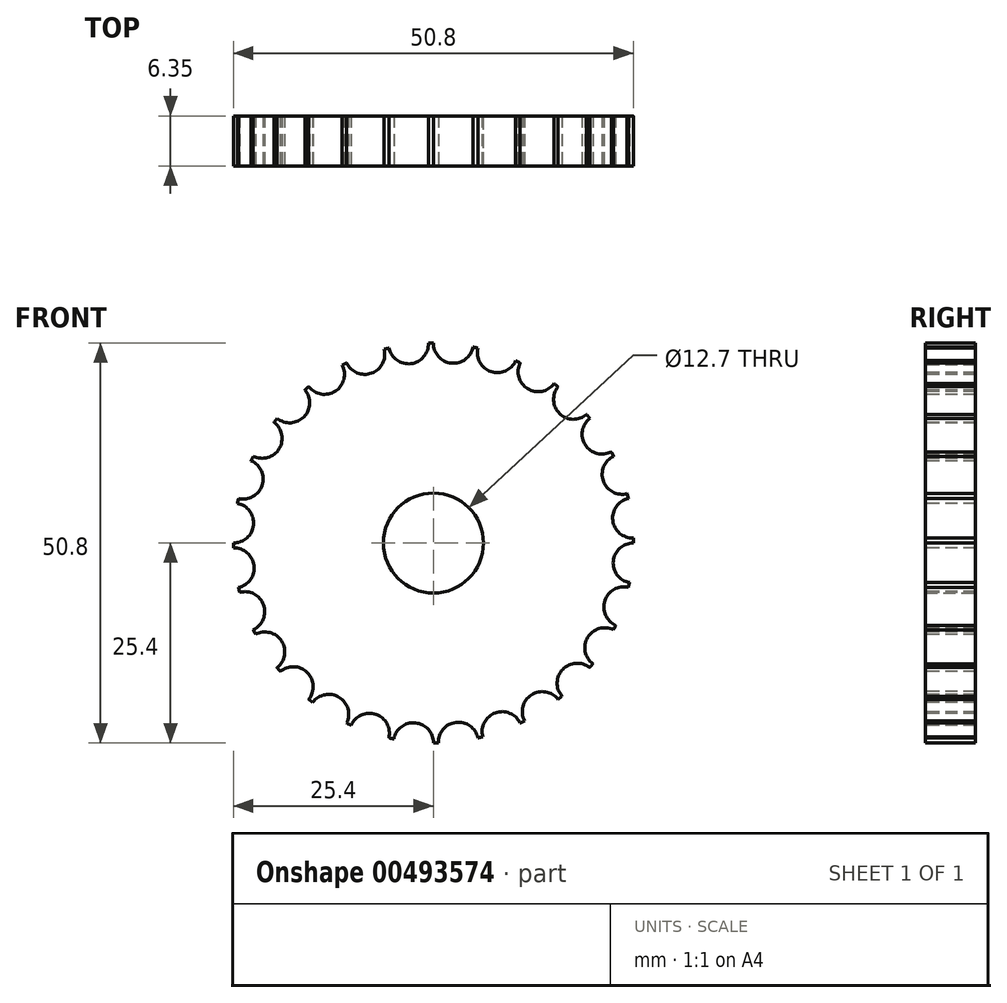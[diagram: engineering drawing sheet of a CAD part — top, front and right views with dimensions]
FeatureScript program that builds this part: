
annotation { "Feature Type Name" : "Feature", "Feature Type Description" : "" }
export const myFeature = defineFeature(function(context is Context, id is Id, definition is map)
    precondition{}
    {
        {
            var Q0;
            Q0=qCreatedBy(makeId("Front.planeOp"),FACE);
            var sketch = newSketch(context, id + "F0", { "sketchPlane" : qUnion([Q0])});
            skCircle(sketch, "E0", {"center": v(0, 0) * mm, "radius": 6.35 * mm});
            skCircle(sketch, "E1", {"center": v(0, 0) * mm, "radius": 25.4 * mm});
            skSolve(sketch);
        }
        {
            var Q0;
            Q0 = qSketchRegion(id + "F0", true);
            extrude(context, id + "F1", {"entities" : qUnion([Q0]), "depth" : 6.35 * mm, "offsetDistance" : 25.4 * mm});
        }
        {
            var Q0;
            Q0=makeQuery(id+"F1.opExtrude","CAP_FACE",FACE,{"disambiguationData":[OSD([sQuery(id+"F0.wireOp",EDGE,"E0"),sQuery(id+"F0.wireOp",EDGE,"E1")])],"isStart":false});
            var sketch = newSketch(context, id + "F2", { "sketchPlane" : qUnion([Q0])});
            skArc(sketch, "E2", {"start": v(0, 25.4) * mm, "mid": v(2.29, 22.85) * mm, "end": v(5.03, 24.9) * mm});
            skCircle(sketch, "E3", {"center": v(0, 0) * mm, "radius": 25.4 * mm});
            skArc(sketch, "E4.1.0", {"start": v(-5.65, 24.76) * mm, "mid": v(-2.86, 22.79) * mm, "end": v(-0.63, 25.4) * mm});
            skArc(sketch, "E4.2.0", {"start": v(-11.02, 22.88) * mm, "mid": v(-7.85, 21.58) * mm, "end": v(-6.27, 24.61) * mm});
            skArc(sketch, "E4.3.0", {"start": v(-15.84, 19.86) * mm, "mid": v(-12.46, 19.3) * mm, "end": v(-11.59, 22.6) * mm});
            skArc(sketch, "E4.4.0", {"start": v(-19.86, 15.84) * mm, "mid": v(-16.44, 16.04) * mm, "end": v(-16.33, 19.46) * mm});
            skArc(sketch, "E4.5.0", {"start": v(-22.88, 11.02) * mm, "mid": v(-19.6, 11.98) * mm, "end": v(-20.25, 15.34) * mm});
            skArc(sketch, "E4.6.0", {"start": v(-24.76, 5.65) * mm, "mid": v(-21.77, 7.31) * mm, "end": v(-23.15, 10.45) * mm});
            skArc(sketch, "E4.7.0", {"start": v(-25.4, 0) * mm, "mid": v(-22.85, 2.29) * mm, "end": v(-24.9, 5.03) * mm});
            skArc(sketch, "E4.8.0", {"start": v(-24.76, -5.65) * mm, "mid": v(-22.79, -2.86) * mm, "end": v(-25.4, -0.63) * mm});
            skArc(sketch, "E4.9.0", {"start": v(-22.88, -11.02) * mm, "mid": v(-21.58, -7.85) * mm, "end": v(-24.61, -6.27) * mm});
            skArc(sketch, "E4.10.0", {"start": v(-19.86, -15.84) * mm, "mid": v(-19.3, -12.46) * mm, "end": v(-22.6, -11.59) * mm});
            skArc(sketch, "E4.11.0", {"start": v(-15.84, -19.86) * mm, "mid": v(-16.04, -16.44) * mm, "end": v(-19.46, -16.33) * mm});
            skArc(sketch, "E4.12.0", {"start": v(-11.02, -22.88) * mm, "mid": v(-11.98, -19.6) * mm, "end": v(-15.34, -20.25) * mm});
            skArc(sketch, "E4.13.0", {"start": v(-5.65, -24.76) * mm, "mid": v(-7.31, -21.77) * mm, "end": v(-10.45, -23.15) * mm});
            skArc(sketch, "E4.14.0", {"start": v(0, -25.4) * mm, "mid": v(-2.29, -22.85) * mm, "end": v(-5.03, -24.9) * mm});
            skArc(sketch, "E4.15.0", {"start": v(5.65, -24.76) * mm, "mid": v(2.86, -22.79) * mm, "end": v(0.63, -25.4) * mm});
            skArc(sketch, "E4.16.0", {"start": v(11.02, -22.88) * mm, "mid": v(7.85, -21.58) * mm, "end": v(6.27, -24.61) * mm});
            skArc(sketch, "E4.17.0", {"start": v(15.84, -19.86) * mm, "mid": v(12.46, -19.3) * mm, "end": v(11.59, -22.6) * mm});
            skArc(sketch, "E4.18.0", {"start": v(19.86, -15.84) * mm, "mid": v(16.44, -16.04) * mm, "end": v(16.33, -19.46) * mm});
            skArc(sketch, "E4.19.0", {"start": v(22.88, -11.02) * mm, "mid": v(19.6, -11.98) * mm, "end": v(20.25, -15.34) * mm});
            skArc(sketch, "E4.20.0", {"start": v(24.76, -5.65) * mm, "mid": v(21.77, -7.31) * mm, "end": v(23.15, -10.45) * mm});
            skArc(sketch, "E4.21.0", {"start": v(25.4, 0) * mm, "mid": v(22.85, -2.29) * mm, "end": v(24.9, -5.03) * mm});
            skArc(sketch, "E5.2.22.0", {"start": v(24.76, 5.65) * mm, "mid": v(22.79, 2.86) * mm, "end": v(25.4, 0.63) * mm});
            skArc(sketch, "E6.2.23.0", {"start": v(22.88, 11.02) * mm, "mid": v(21.58, 7.85) * mm, "end": v(24.61, 6.27) * mm});
            skArc(sketch, "E7.2.24.0", {"start": v(19.86, 15.84) * mm, "mid": v(19.3, 12.46) * mm, "end": v(22.6, 11.59) * mm});
            skArc(sketch, "E8.2.25.0", {"start": v(15.84, 19.86) * mm, "mid": v(16.04, 16.44) * mm, "end": v(19.46, 16.33) * mm});
            skArc(sketch, "E9.2.26.0", {"start": v(11.02, 22.88) * mm, "mid": v(11.98, 19.6) * mm, "end": v(15.34, 20.25) * mm});
            skArc(sketch, "E9.2.27.0", {"start": v(5.65, 24.76) * mm, "mid": v(7.31, 21.77) * mm, "end": v(10.45, 23.15) * mm});
            skSolve(sketch);
        }
        {
            var Q0;
            {var subQ0=sQuery(id+"F2.wireOp",EDGE,"E4.1.0");Q0=makeQuery(id+"F2.imprint","IMPRINT",FACE,{"disambiguationData":[TD([[makeQuery(id+"F2.imprint","IMPRINT",EDGE,{"derivedFrom":subQ0}),1.0]])]});}
            var Q1;
            {var subQ0=sQuery(id+"F2.wireOp",EDGE,"E2");Q1=makeQuery(id+"F2.imprint","IMPRINT",FACE,{"disambiguationData":[TD([[makeQuery(id+"F2.imprint","IMPRINT",EDGE,{"derivedFrom":subQ0}),1.0]])]});}
            var Q2;
            {var subQ0=sQuery(id+"F2.wireOp",EDGE,"E4.21.0");Q2=makeQuery(id+"F2.imprint","IMPRINT",FACE,{"disambiguationData":[TD([[makeQuery(id+"F2.imprint","IMPRINT",EDGE,{"derivedFrom":subQ0}),1.0]])]});}
            var Q3;
            {var subQ0=sQuery(id+"F2.wireOp",EDGE,"E4.20.0");Q3=makeQuery(id+"F2.imprint","IMPRINT",FACE,{"disambiguationData":[TD([[makeQuery(id+"F2.imprint","IMPRINT",EDGE,{"derivedFrom":subQ0}),1.0]])]});}
            var Q4;
            {var subQ0=sQuery(id+"F2.wireOp",EDGE,"E4.19.0");Q4=makeQuery(id+"F2.imprint","IMPRINT",FACE,{"disambiguationData":[TD([[makeQuery(id+"F2.imprint","IMPRINT",EDGE,{"derivedFrom":subQ0}),1.0]])]});}
            var Q5;
            {var subQ0=sQuery(id+"F2.wireOp",EDGE,"E4.18.0");Q5=makeQuery(id+"F2.imprint","IMPRINT",FACE,{"disambiguationData":[TD([[makeQuery(id+"F2.imprint","IMPRINT",EDGE,{"derivedFrom":subQ0}),1.0]])]});}
            var Q6;
            {var subQ0=sQuery(id+"F2.wireOp",EDGE,"E4.17.0");Q6=makeQuery(id+"F2.imprint","IMPRINT",FACE,{"disambiguationData":[TD([[makeQuery(id+"F2.imprint","IMPRINT",EDGE,{"derivedFrom":subQ0}),1.0]])]});}
            var Q7;
            {var subQ0=sQuery(id+"F2.wireOp",EDGE,"E4.16.0");Q7=makeQuery(id+"F2.imprint","IMPRINT",FACE,{"disambiguationData":[TD([[makeQuery(id+"F2.imprint","IMPRINT",EDGE,{"derivedFrom":subQ0}),1.0]])]});}
            var Q8;
            {var subQ0=sQuery(id+"F2.wireOp",EDGE,"E4.15.0");Q8=makeQuery(id+"F2.imprint","IMPRINT",FACE,{"disambiguationData":[TD([[makeQuery(id+"F2.imprint","IMPRINT",EDGE,{"derivedFrom":subQ0}),1.0]])]});}
            var Q9;
            {var subQ0=sQuery(id+"F2.wireOp",EDGE,"E4.14.0");Q9=makeQuery(id+"F2.imprint","IMPRINT",FACE,{"disambiguationData":[TD([[makeQuery(id+"F2.imprint","IMPRINT",EDGE,{"derivedFrom":subQ0}),1.0]])]});}
            var Q10;
            {var subQ0=sQuery(id+"F2.wireOp",EDGE,"E4.13.0");Q10=makeQuery(id+"F2.imprint","IMPRINT",FACE,{"disambiguationData":[TD([[makeQuery(id+"F2.imprint","IMPRINT",EDGE,{"derivedFrom":subQ0}),1.0]])]});}
            var Q11;
            {var subQ0=sQuery(id+"F2.wireOp",EDGE,"E4.12.0");Q11=makeQuery(id+"F2.imprint","IMPRINT",FACE,{"disambiguationData":[TD([[makeQuery(id+"F2.imprint","IMPRINT",EDGE,{"derivedFrom":subQ0}),1.0]])]});}
            var Q12;
            {var subQ0=sQuery(id+"F2.wireOp",EDGE,"E4.11.0");Q12=makeQuery(id+"F2.imprint","IMPRINT",FACE,{"disambiguationData":[TD([[makeQuery(id+"F2.imprint","IMPRINT",EDGE,{"derivedFrom":subQ0}),1.0]])]});}
            var Q13;
            {var subQ0=sQuery(id+"F2.wireOp",EDGE,"E4.10.0");Q13=makeQuery(id+"F2.imprint","IMPRINT",FACE,{"disambiguationData":[TD([[makeQuery(id+"F2.imprint","IMPRINT",EDGE,{"derivedFrom":subQ0}),1.0]])]});}
            var Q14;
            {var subQ0=sQuery(id+"F2.wireOp",EDGE,"E4.9.0");Q14=makeQuery(id+"F2.imprint","IMPRINT",FACE,{"disambiguationData":[TD([[makeQuery(id+"F2.imprint","IMPRINT",EDGE,{"derivedFrom":subQ0}),1.0]])]});}
            var Q15;
            {var subQ0=sQuery(id+"F2.wireOp",EDGE,"E4.8.0");Q15=makeQuery(id+"F2.imprint","IMPRINT",FACE,{"disambiguationData":[TD([[makeQuery(id+"F2.imprint","IMPRINT",EDGE,{"derivedFrom":subQ0}),1.0]])]});}
            var Q16;
            {var subQ0=sQuery(id+"F2.wireOp",EDGE,"E4.7.0");Q16=makeQuery(id+"F2.imprint","IMPRINT",FACE,{"disambiguationData":[TD([[makeQuery(id+"F2.imprint","IMPRINT",EDGE,{"derivedFrom":subQ0}),1.0]])]});}
            var Q17;
            {var subQ0=sQuery(id+"F2.wireOp",EDGE,"E4.6.0");Q17=makeQuery(id+"F2.imprint","IMPRINT",FACE,{"disambiguationData":[TD([[makeQuery(id+"F2.imprint","IMPRINT",EDGE,{"derivedFrom":subQ0}),1.0]])]});}
            var Q18;
            {var subQ0=sQuery(id+"F2.wireOp",EDGE,"E4.5.0");Q18=makeQuery(id+"F2.imprint","IMPRINT",FACE,{"disambiguationData":[TD([[makeQuery(id+"F2.imprint","IMPRINT",EDGE,{"derivedFrom":subQ0}),1.0]])]});}
            var Q19;
            {var subQ0=sQuery(id+"F2.wireOp",EDGE,"E4.4.0");Q19=makeQuery(id+"F2.imprint","IMPRINT",FACE,{"disambiguationData":[TD([[makeQuery(id+"F2.imprint","IMPRINT",EDGE,{"derivedFrom":subQ0}),1.0]])]});}
            var Q20;
            {var subQ0=sQuery(id+"F2.wireOp",EDGE,"E4.3.0");Q20=makeQuery(id+"F2.imprint","IMPRINT",FACE,{"disambiguationData":[TD([[makeQuery(id+"F2.imprint","IMPRINT",EDGE,{"derivedFrom":subQ0}),1.0]])]});}
            var Q21;
            {var subQ0=sQuery(id+"F2.wireOp",EDGE,"E4.2.0");Q21=makeQuery(id+"F2.imprint","IMPRINT",FACE,{"disambiguationData":[TD([[makeQuery(id+"F2.imprint","IMPRINT",EDGE,{"derivedFrom":subQ0}),1.0]])]});}
            var Q22;
            {var subQ0=sQuery(id+"F2.wireOp",EDGE,"E9.2.27.0");Q22=makeQuery(id+"F2.imprint","IMPRINT",FACE,{"disambiguationData":[TD([[makeQuery(id+"F2.imprint","IMPRINT",EDGE,{"derivedFrom":subQ0}),1.0]])]});}
            var Q23;
            {var subQ0=sQuery(id+"F2.wireOp",EDGE,"E9.2.26.0");Q23=makeQuery(id+"F2.imprint","IMPRINT",FACE,{"disambiguationData":[TD([[makeQuery(id+"F2.imprint","IMPRINT",EDGE,{"derivedFrom":subQ0}),1.0]])]});}
            var Q24;
            {var subQ0=sQuery(id+"F2.wireOp",EDGE,"E8.2.25.0");Q24=makeQuery(id+"F2.imprint","IMPRINT",FACE,{"disambiguationData":[TD([[makeQuery(id+"F2.imprint","IMPRINT",EDGE,{"derivedFrom":subQ0}),1.0]])]});}
            var Q25;
            {var subQ0=sQuery(id+"F2.wireOp",EDGE,"E7.2.24.0");Q25=makeQuery(id+"F2.imprint","IMPRINT",FACE,{"disambiguationData":[TD([[makeQuery(id+"F2.imprint","IMPRINT",EDGE,{"derivedFrom":subQ0}),1.0]])]});}
            var Q26;
            {var subQ0=sQuery(id+"F2.wireOp",EDGE,"E6.2.23.0");Q26=makeQuery(id+"F2.imprint","IMPRINT",FACE,{"disambiguationData":[TD([[makeQuery(id+"F2.imprint","IMPRINT",EDGE,{"derivedFrom":subQ0}),1.0]])]});}
            var Q27;
            {var subQ0=sQuery(id+"F2.wireOp",EDGE,"E5.2.22.0");Q27=makeQuery(id+"F2.imprint","IMPRINT",FACE,{"disambiguationData":[TD([[makeQuery(id+"F2.imprint","IMPRINT",EDGE,{"derivedFrom":subQ0}),1.0]])]});}
            extrude(context, id + "F3", {"entities" : qUnion([Q0, Q1, Q2, Q3, Q4, Q5, Q6, Q7, Q8, Q9, Q10, Q11, Q12, Q13, Q14, Q15, Q16, Q17, Q18, Q19, Q20, Q21, Q22, Q23, Q24, Q25, Q26, Q27]), "operationType" : NewBodyOperationType.REMOVE, "endBound" : BoundingType.THROUGH_ALL, "oppositeDirection" : true, "depth" : 25.4 * mm, "offsetDistance" : 25.4 * mm});
        }
    });
